# Revit family: Towel_Ring-Grohe-Defined-40972_Series
name_source: partatom
category: Specialty Equipment
units: mm (PartAtom-declared; Revit-internal decimal feet)

## family parameters
Cut with Voids When Loaded = No
Host = Face
OmniClass Number = 23.40.20.21.27
OmniClass Title = Towel Bars
Part Type = Normal
Room Calculation Point = No
Round Connector Dimension = Use Diameter
Shared = Yes

## types (2) — shared parameters
Assembly Code = C1030200
CalGreen Compliant = Yes
Default Elevation = 40"
Height = 9/16"
Installation Type = Wall Mounted
Length = 3 3/8"
Manufacturer = Grohe
Product Documentation Link = https://americanstandard.box.com
Product Page URL = https://www.grohe.us
Revised Date = 06/07/2023
URL = https://www.grohe.us
Width = 8 1/16"

## per-type parameters (varying)
| type | Description | Finish | Material |
| 40972000 | DEFINED Towel Ring Starlight Chrome | Metal-Grohe-000-Starlight Chrome | Metal-Grohe-000-Starlight Chrome |
| 40972EN0 | DEFINED Towel Ring Brushed Nickel | Metal-Grohe-EN0-Brushed Nickel | Metal-Grohe-EN0-Brushed Nickel |

note: column(s) folded — value = type name in every type: Model

## geometry (parser evidence)
native form markers: Sweep x4
no freeform markers — native parametric forms only
